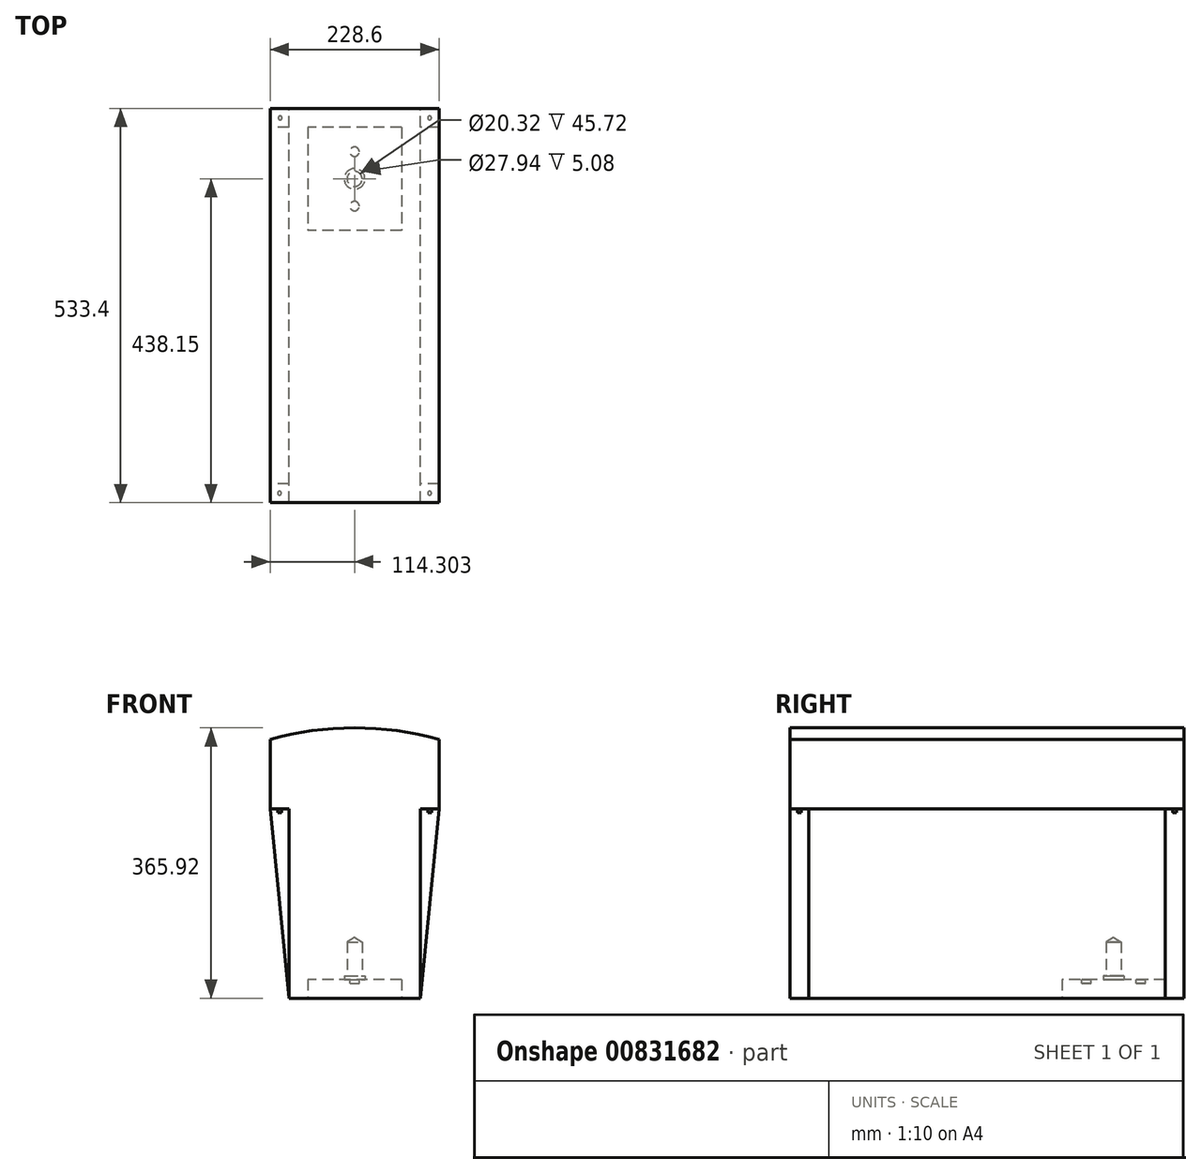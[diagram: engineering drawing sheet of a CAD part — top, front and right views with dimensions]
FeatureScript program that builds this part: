
annotation { "Feature Type Name" : "Feature", "Feature Type Description" : "" }
export const myFeature = defineFeature(function(context is Context, id is Id, definition is map)
    precondition{}
    {
        {
            var Q0;
            Q0=qCreatedBy(makeId("Front.planeOp"),FACE);
            var sketch = newSketch(context, id + "F0", { "sketchPlane" : qUnion([Q0])});
            skLineSegment(sketch, "E0", {"start": v(-155.23, 160.77) * mm, "end": v(73.37, 160.77) * mm});
            skLineSegment(sketch, "E1", {"start": v(73.37, 160.77) * mm, "end": v(73.37, 66.79) * mm});
            skLineSegment(sketch, "E2", {"start": v(73.37, 66.79) * mm, "end": v(47.97, -189.75) * mm});
            skLineSegment(sketch, "E3", {"start": v(47.97, -189.75) * mm, "end": v(-129.83, -189.75) * mm});
            skLineSegment(sketch, "E4", {"start": v(-129.83, -189.75) * mm, "end": v(-155.23, 66.79) * mm});
            skLineSegment(sketch, "E5", {"start": v(-155.23, 66.79) * mm, "end": v(-155.23, 160.77) * mm});
            skPoint(sketch, "E6.endSnap0", {"position": v(-129.83, -61.54) * mm});
            skPoint(sketch, "E7.orphan", {"position": v(-129.83, 66.67) * mm});
            skPoint(sketch, "E6.end.orphan", {"position": v(-149.99, -61.54) * mm});
            skLineSegment(sketch, "E8", {"start": v(-129.83, -189.75) * mm, "end": v(-129.83, 51.04) * mm});
            skLineSegment(sketch, "E9", {"start": v(47.97, -189.75) * mm, "end": v(47.97, 51.04) * mm});
            skLineSegment(sketch, "E10", {"start": v(47.97, 51.04) * mm, "end": v(71.81, 51.04) * mm});
            skLineSegment(sketch, "E11", {"start": v(-129.83, 51.04) * mm, "end": v(-153.67, 51.04) * mm});
            skSolve(sketch);
        }
        {
            var Q0;
            Q0 = qSketchRegion(id + "F0", true);
            extrude(context, id + "F1", {"entities" : qUnion([Q0]), "depth" : 533.4 * mm, "offsetDistance" : 25.4 * mm});
        }
        {
            var Q0;
            Q0=makeQuery(id+"F1.opExtrude","CAP_FACE",FACE,{"disambiguationData":[OSD([sQuery(id+"F0.wireOp",EDGE,"E0"),sQuery(id+"F0.wireOp",EDGE,"E1"),sQuery(id+"F0.wireOp",EDGE,"E2"),sQuery(id+"F0.wireOp",EDGE,"E3"),sQuery(id+"F0.wireOp",EDGE,"E4"),sQuery(id+"F0.wireOp",EDGE,"E5")])],"isStart":false});
            var sketch = newSketch(context, id + "F2", { "sketchPlane" : qUnion([Q0])});
            skLineSegment(sketch, "E12", {"start": v(-155.23, 66.79) * mm, "end": v(-129.83, 66.79) * mm});
            skLineSegment(sketch, "E13", {"start": v(-129.83, 66.79) * mm, "end": v(-129.83, -189.75) * mm});
            skLineSegment(sketch, "E14", {"start": v(-129.83, -189.75) * mm, "end": v(-155.23, 66.79) * mm});
            skSolve(sketch);
        }
        {
            var Q0;
            Q0 = qSketchRegion(id + "F2", true);
            extrude(context, id + "F3", {"entities" : qUnion([Q0]), "operationType" : NewBodyOperationType.REMOVE, "oppositeDirection" : true, "depth" : 25.4 * mm, "offsetDistance" : 25.4 * mm});
        }
        {
            var Q0;
            Q0=makeQuery(id+"F1.opExtrude","CAP_FACE",FACE,{"disambiguationData":[OSD([sQuery(id+"F0.wireOp",EDGE,"E0"),sQuery(id+"F0.wireOp",EDGE,"E1"),sQuery(id+"F0.wireOp",EDGE,"E2"),sQuery(id+"F0.wireOp",EDGE,"E3"),sQuery(id+"F0.wireOp",EDGE,"E4"),sQuery(id+"F0.wireOp",EDGE,"E5")])],"isStart":false});
            var sketch = newSketch(context, id + "F4", { "sketchPlane" : qUnion([Q0])});
            skLineSegment(sketch, "E15", {"start": v(47.97, -189.75) * mm, "end": v(73.37, 66.79) * mm});
            skLineSegment(sketch, "E16", {"start": v(47.97, -189.75) * mm, "end": v(47.97, 66.79) * mm});
            skLineSegment(sketch, "E17", {"start": v(73.37, 66.79) * mm, "end": v(47.97, 66.79) * mm});
            skSolve(sketch);
        }
        {
            var Q0;
            Q0 = qSketchRegion(id + "F4", true);
            extrude(context, id + "F5", {"entities" : qUnion([Q0]), "operationType" : NewBodyOperationType.REMOVE, "oppositeDirection" : true, "depth" : 25.4 * mm, "offsetDistance" : 25.4 * mm});
        }
        {
            var Q0;
            Q0=makeQuery(id+"F1.opExtrude","CAP_FACE",FACE,{"disambiguationData":[OSD([sQuery(id+"F0.wireOp",EDGE,"E0"),sQuery(id+"F0.wireOp",EDGE,"E1"),sQuery(id+"F0.wireOp",EDGE,"E2"),sQuery(id+"F0.wireOp",EDGE,"E3"),sQuery(id+"F0.wireOp",EDGE,"E4"),sQuery(id+"F0.wireOp",EDGE,"E5")])],"isStart":true});
            var sketch = newSketch(context, id + "F6", { "sketchPlane" : qUnion([Q0])});
            skLineSegment(sketch, "E18", {"start": v(-73.37, 66.79) * mm, "end": v(-47.97, -189.75) * mm});
            skLineSegment(sketch, "E19", {"start": v(-47.97, -189.75) * mm, "end": v(-47.97, 66.79) * mm});
            skLineSegment(sketch, "E20", {"start": v(-47.97, 66.79) * mm, "end": v(-73.37, 66.79) * mm});
            skLineSegment(sketch, "E21", {"start": v(129.83, -189.75) * mm, "end": v(155.23, 66.79) * mm});
            skLineSegment(sketch, "E22", {"start": v(155.23, 66.79) * mm, "end": v(129.83, 66.79) * mm});
            skLineSegment(sketch, "E23", {"start": v(129.83, 66.79) * mm, "end": v(129.83, -189.75) * mm});
            skSolve(sketch);
        }
        {
            var Q0;
            Q0 = qSketchRegion(id + "F6", true);
            extrude(context, id + "F7", {"entities" : qUnion([Q0]), "operationType" : NewBodyOperationType.REMOVE, "oppositeDirection" : true, "depth" : 25.4 * mm, "offsetDistance" : 25.4 * mm});
        }
        {
            var Q0;
            Q0=makeQuery(id+"F1.opExtrude","SWEPT_FACE",FACE,{"disambiguationData":[OSD([sQuery(id+"F0.wireOp",EDGE,"E3")])]});
            var sketch = newSketch(context, id + "F8", { "sketchPlane" : qUnion([Q0])});
            skLineSegment(sketch, "E24", {"start": v(-129.83, 0) * mm, "end": v(-129.83, 25.4) * mm});
            skLineSegment(sketch, "E25", {"start": v(47.97, 25.4) * mm, "end": v(47.97, 165.1) * mm});
            skLineSegment(sketch, "E26", {"start": v(47.97, 165.1) * mm, "end": v(-129.83, 165.1) * mm});
            skLineSegment(sketch, "E27", {"start": v(-129.83, 25.4) * mm, "end": v(-104.43, 25.4) * mm});
            skLineSegment(sketch, "E28", {"start": v(47.97, 25.4) * mm, "end": v(22.57, 25.4) * mm});
            skLineSegment(sketch, "E29", {"start": v(22.57, 25.4) * mm, "end": v(22.57, 165.1) * mm});
            skLineSegment(sketch, "E30", {"start": v(-104.43, 25.4) * mm, "end": v(-104.43, 165.1) * mm});
            skLineSegment(sketch, "E31", {"start": v(-104.43, 165.1) * mm, "end": v(22.57, 165.1) * mm});
            skLineSegment(sketch, "E32", {"start": v(22.57, 25.4) * mm, "end": v(-104.43, 25.4) * mm});
            skSolve(sketch);
        }
        {
            var Q0;
            Q0=makeQuery(id+"F8.imprint","IMPRINT",FACE,{"disambiguationData":[TD([[makeQuery(id+"F8.imprint","IMPRINT",EDGE,{"derivedFrom":sQuery(id+"F8.wireOp",EDGE,"E29")}),1.0]])]});
            var sketch = newSketch(context, id + "F9", { "sketchPlane" : qUnion([Q0])});
            skSolve(sketch);
        }
        {
            var Q0;
            Q0=makeQuery(id+"F8.imprint","IMPRINT",FACE,{"disambiguationData":[TD([[makeQuery(id+"F8.imprint","IMPRINT",EDGE,{"derivedFrom":sQuery(id+"F8.wireOp",EDGE,"E29")}),1.0]])]});
            extrude(context, id + "F10", {"entities" : qUnion([Q0]), "operationType" : NewBodyOperationType.REMOVE, "oppositeDirection" : true, "depth" : 25.4 * mm, "offsetDistance" : 25.4 * mm});
        }
        {
            var Q0;
            Q0=makeQuery(id+"F9.imprint","IMPRINT",FACE,{"disambiguationData":[TD([[makeQuery(id+"F9.imprint","IMPRINT",EDGE,{"derivedFrom":makeQuery(id+"F8.imprint","IMPRINT",EDGE,{"derivedFrom":sQuery(id+"F8.wireOp",EDGE,"E29")})}),1.0]])]});
            cPlane(context, id + "F11", {"entities" : qUnion([Q0]), "cplaneType" : CPlaneType.OFFSET, "offset" : 25.4 * mm, "oppositeDirection" : true, "width" : 152.4 * mm, "height" : 152.4 * mm});
        }
        {
            var Q0;
            Q0=qCreatedBy(id+"F11.planeOp",FACE);
            var sketch = newSketch(context, id + "F12", { "sketchPlane" : qUnion([Q0])});
            skPoint(sketch, "E33", {"position": v(-40.93, 95.25) * mm});
            skSolve(sketch);
        }
        {
            var Q0;
            Q0=sQuery(id+"F12.wireOp",VERTEX,"E33");
            var Q1;
            Q1=makeQuery(id+"F1.opExtrude","SWEPT_BODY",BODY,{"disambiguationData":[OSD([sQuery(id+"F0.wireOp",EDGE,"E0"),sQuery(id+"F0.wireOp",EDGE,"E1"),sQuery(id+"F0.wireOp",EDGE,"E2"),sQuery(id+"F0.wireOp",EDGE,"E3"),sQuery(id+"F0.wireOp",EDGE,"E4"),sQuery(id+"F0.wireOp",EDGE,"E5")])]});
            hole(context, id + "F13", {"style" : HoleStyle.C_BORE, "endStyle" : HoleEndStyle.BLIND, "holeDiameter" : 20.32 * mm, "cBoreDiameter" : 27.94 * mm, "cBoreDepth" : 5.08 * mm, "majorDiameter" : 6.35 * mm, "holeDepth" : 50.8 * mm, "isTappedThrough" : true, "tappedDepth" : 12.7 * mm, "tapClearance" : 3, "locations" : qUnion([Q0]), "scope" : qUnion([Q1])});
        }
        {
            var Q0;
            Q0=qCreatedBy(id+"F11.planeOp",FACE);
            var sketch = newSketch(context, id + "F14", { "sketchPlane" : qUnion([Q0])});
            skPoint(sketch, "E34", {"position": v(-40.93, 132.08) * mm});
            skPoint(sketch, "E35", {"position": v(-40.93, 58.42) * mm});
            skCircle(sketch, "E36", {"center": v(-40.93, 132.08) * mm, "radius": 6.35 * mm});
            skCircle(sketch, "E37", {"center": v(-40.93, 58.42) * mm, "radius": 6.35 * mm});
            skSolve(sketch);
        }
        {
            var Q0;
            Q0 = qSketchRegion(id + "F14", true);
            extrude(context, id + "F15", {"entities" : qUnion([Q0]), "operationType" : NewBodyOperationType.ADD, "depth" : 5.08 * mm, "offsetDistance" : 25.4 * mm});
        }
        {
            var Q0;
            Q0=makeQuery(id+"F7.boolean.opBoolean","COPY",FACE,{"derivedFrom":makeQuery(id+"F7.opExtrude","SWEPT_FACE",FACE,{"disambiguationData":[OSD([sQuery(id+"F6.wireOp",EDGE,"E20")])]})});
            var sketch = newSketch(context, id + "F16", { "sketchPlane" : qUnion([Q0])});
            skPoint(sketch, "E38", {"position": v(60.67, 12.7) * mm});
            skPoint(sketch, "E38.positionSnap0", {"position": v(60.67, 25.4) * mm});
            skCircle(sketch, "E39", {"center": v(60.67, 12.7) * mm, "radius": 2.54 * mm});
            skSolve(sketch);
        }
        {
            var Q0;
            Q0=makeQuery(id+"F16.imprint","IMPRINT",FACE,{"disambiguationData":[TD([[makeQuery(id+"F16.imprint","IMPRINT",EDGE,{"derivedFrom":sQuery(id+"F16.wireOp",EDGE,"E39")}),1.0]])]});
            extrude(context, id + "F17", {"entities" : qUnion([Q0]), "operationType" : NewBodyOperationType.ADD, "depth" : 5.08 * mm, "offsetDistance" : 25.4 * mm});
        }
        {
            var Q0;
            Q0=makeQuery(id+"F7.boolean.opBoolean","COPY",FACE,{"derivedFrom":makeQuery(id+"F7.opExtrude","SWEPT_FACE",FACE,{"disambiguationData":[OSD([sQuery(id+"F6.wireOp",EDGE,"E22")])]})});
            var sketch = newSketch(context, id + "F18", { "sketchPlane" : qUnion([Q0])});
            skPoint(sketch, "E40", {"position": v(-141.65, 12.7) * mm});
            skCircle(sketch, "E41", {"center": v(-141.65, 12.7) * mm, "radius": 2.54 * mm});
            skSolve(sketch);
        }
        {
            var Q0;
            Q0 = qSketchRegion(id + "F18", true);
            extrude(context, id + "F19", {"entities" : qUnion([Q0]), "operationType" : NewBodyOperationType.ADD, "depth" : 5.08 * mm, "offsetDistance" : 25.4 * mm});
        }
        {
            var Q0;
            Q0=makeQuery(id+"F5.boolean.opBoolean","COPY",FACE,{"derivedFrom":makeQuery(id+"F5.opExtrude","SWEPT_FACE",FACE,{"disambiguationData":[OSD([sQuery(id+"F4.wireOp",EDGE,"E17")])]})});
            var sketch = newSketch(context, id + "F20", { "sketchPlane" : qUnion([Q0])});
            skPoint(sketch, "E42", {"position": v(60.67, 520.7) * mm});
            skCircle(sketch, "E43", {"center": v(60.67, 520.7) * mm, "radius": 2.54 * mm});
            skSolve(sketch);
        }
        {
            var Q0;
            Q0 = qSketchRegion(id + "F20", true);
            extrude(context, id + "F21", {"entities" : qUnion([Q0]), "operationType" : NewBodyOperationType.ADD, "depth" : 5.08 * mm, "offsetDistance" : 25.4 * mm});
        }
        {
            var Q0;
            Q0=makeQuery(id+"F3.boolean.opBoolean","COPY",FACE,{"derivedFrom":makeQuery(id+"F3.opExtrude","SWEPT_FACE",FACE,{"disambiguationData":[OSD([sQuery(id+"F2.wireOp",EDGE,"E12")])]})});
            var sketch = newSketch(context, id + "F22", { "sketchPlane" : qUnion([Q0])});
            skPoint(sketch, "E44", {"position": v(-142.53, 520.7) * mm});
            skCircle(sketch, "E45", {"center": v(-142.53, 520.7) * mm, "radius": 2.54 * mm});
            skSolve(sketch);
        }
        {
            var Q0;
            Q0 = qSketchRegion(id + "F22", true);
            extrude(context, id + "F23", {"entities" : qUnion([Q0]), "operationType" : NewBodyOperationType.ADD, "depth" : 5.08 * mm, "offsetDistance" : 25.4 * mm});
        }
        {
            var Q0;
            Q0=makeQuery(id+"F1.opExtrude","CAP_FACE",FACE,{"disambiguationData":[OSD([sQuery(id+"F0.wireOp",EDGE,"E0"),sQuery(id+"F0.wireOp",EDGE,"E1"),sQuery(id+"F0.wireOp",EDGE,"E2"),sQuery(id+"F0.wireOp",EDGE,"E3"),sQuery(id+"F0.wireOp",EDGE,"E4"),sQuery(id+"F0.wireOp",EDGE,"E5")])],"isStart":true});
            var sketch = newSketch(context, id + "F24", { "sketchPlane" : qUnion([Q0])});
            skArc(sketch, "E46", {"start": v(155.23, 160.77) * mm, "mid": v(40.93, 176.17) * mm, "end": v(-73.37, 160.77) * mm});
            skLineSegment(sketch, "E47", {"start": v(-73.37, 160.77) * mm, "end": v(155.23, 160.77) * mm});
            skSolve(sketch);
        }
        {
            var Q0;
            Q0 = qSketchRegion(id + "F24", true);
            extrude(context, id + "F25", {"entities" : qUnion([Q0]), "operationType" : NewBodyOperationType.ADD, "oppositeDirection" : true, "depth" : 533.4 * mm, "offsetDistance" : 25.4 * mm});
        }
    });
